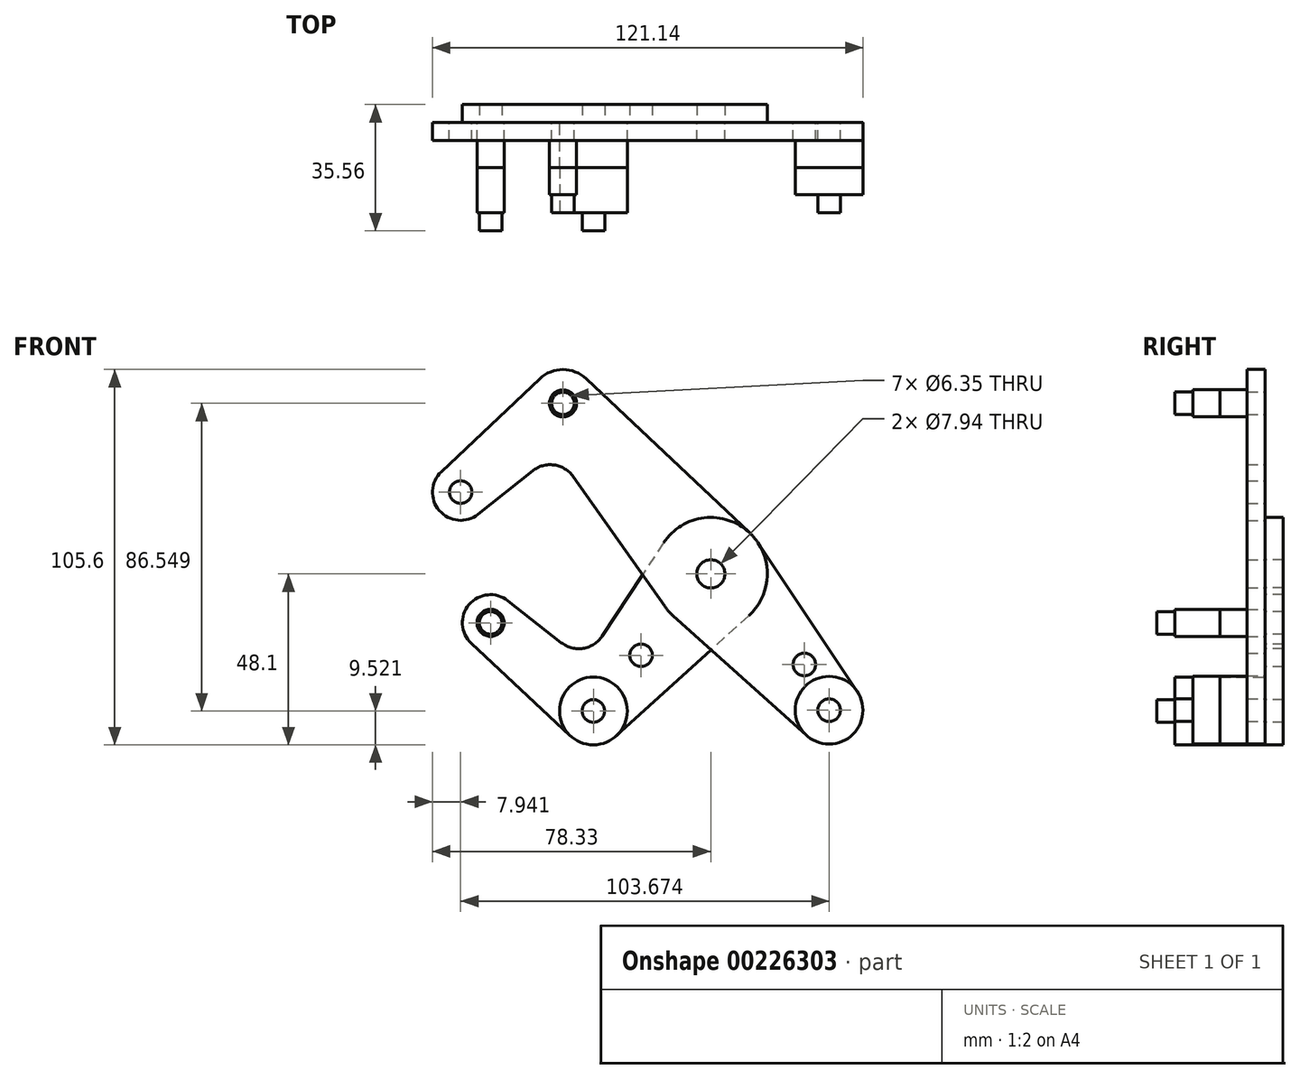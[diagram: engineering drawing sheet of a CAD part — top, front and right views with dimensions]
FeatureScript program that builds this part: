
annotation { "Feature Type Name" : "Feature", "Feature Type Description" : "" }
export const myFeature = defineFeature(function(context is Context, id is Id, definition is map)
    precondition{}
    {
        {
            var Q0;
            Q0=qCreatedBy(makeId("Front.planeOp"),FACE);
            var sketch = newSketch(context, id + "F0", { "sketchPlane" : qUnion([Q0])});
            skLineSegment(sketch, "E0", {"start": v(-41.6, 47.97) * mm, "end": v(41.6, -47.97) * mm, "construction": true});
            skCircle(sketch, "E1", {"center": v(0, 0) * mm, "radius": 3.18 * mm});
            skCircle(sketch, "E2", {"center": v(33.29, -38.38) * mm, "radius": 3.18 * mm});
            skCircle(sketch, "E3", {"center": v(-41.6, 47.97) * mm, "radius": 3.18 * mm});
            skCircle(sketch, "E4", {"center": v(-70.39, 23) * mm, "radius": 3.18 * mm});
            skLineSegment(sketch, "E5", {"start": v(-41.6, 47.97) * mm, "end": v(-70.39, 23) * mm, "construction": true});
            skCircle(sketch, "E6", {"center": v(33.29, -38.38) * mm, "radius": 9.53 * mm});
            skCircle(sketch, "E7", {"center": v(-70.39, 23) * mm, "radius": 7.94 * mm});
            skCircle(sketch, "E8", {"center": v(-41.6, 47.97) * mm, "radius": 9.53 * mm});
            skLineSegment(sketch, "E9", {"start": v(-75.83, 28.78) * mm, "end": v(-48.14, 54.9) * mm});
            skLineSegment(sketch, "E10", {"start": v(-65.44, 16.8) * mm, "end": v(-50.15, 28.98) * mm});
            skCircle(sketch, "E11", {"center": v(0, 0) * mm, "radius": 15.88 * mm});
            skLineSegment(sketch, "E12", {"start": v(-35.07, 54.9) * mm, "end": v(10.9, 11.55) * mm});
            skLineSegment(sketch, "E13", {"start": v(-38.72, 27.35) * mm, "end": v(-12.97, -9.15) * mm});
            skLineSegment(sketch, "E14", {"start": v(-10.6, -11.82) * mm, "end": v(26.93, -45.47) * mm});
            skLineSegment(sketch, "E15", {"start": v(13.2, 8.82) * mm, "end": v(41.2, -33.08) * mm});
            skArc(sketch, "E16.filletArc", {"start": v(-38.72, 27.35) * mm, "mid": v(-44.08, 30.63) * mm, "end": v(-50.15, 28.98) * mm});
            skLineSegment(sketch, "E17", {"start": v(0, 0) * mm, "end": v(-33.05, -38.58) * mm, "construction": true});
            skLineSegment(sketch, "E18", {"start": v(-33.05, -38.58) * mm, "end": v(-61.98, -13.8) * mm, "construction": true});
            skCircle(sketch, "E19", {"center": v(-61.98, -13.8) * mm, "radius": 3.18 * mm});
            skCircle(sketch, "E20", {"center": v(-33.05, -38.58) * mm, "radius": 3.18 * mm});
            skCircle(sketch, "E21", {"center": v(-61.98, -13.8) * mm, "radius": 7.94 * mm});
            skCircle(sketch, "E22", {"center": v(-33.05, -38.58) * mm, "radius": 9.53 * mm});
            skLineSegment(sketch, "E23", {"start": v(-57.08, -7.55) * mm, "end": v(-42.08, -19.35) * mm});
            skLineSegment(sketch, "E24", {"start": v(-67.4, -19.6) * mm, "end": v(-39.54, -45.55) * mm});
            skLineSegment(sketch, "E25", {"start": v(-13.25, 8.74) * mm, "end": v(-30.55, -17.48) * mm});
            skLineSegment(sketch, "E26", {"start": v(10.67, -11.75) * mm, "end": v(-26.65, -45.63) * mm});
            skArc(sketch, "E27.filletArc", {"start": v(-42.08, -19.35) * mm, "mid": v(-35.9, -20.95) * mm, "end": v(-30.55, -17.48) * mm});
            skCircle(sketch, "E28", {"center": v(-19.62, -22.9) * mm, "radius": 3.18 * mm});
            skCircle(sketch, "E29", {"center": v(26.32, -25.5) * mm, "radius": 3.18 * mm});
            skLineSegment(sketch, "E30", {"start": v(26.32, -25.5) * mm, "end": v(23.92, -27.58) * mm, "construction": true});
            skCircle(sketch, "E31", {"center": v(0, 0) * mm, "radius": 3.97 * mm});
            skSolve(sketch);
        }
        {
            var Q0;
            Q0=qCreatedBy(makeId("Front.planeOp"),FACE);
            cPlane(context, id + "F1", {"entities" : qUnion([Q0]), "cplaneType" : CPlaneType.OFFSET, "offset" : 12.7 * mm, "width" : 254 * mm, "height" : 254 * mm});
        }
        {
            var Q0;
            {var subQ0=sQuery(id+"F0.wireOp",EDGE,"E15");Q0=makeQuery(id+"F0.imprint","IMPRINT",FACE,{"disambiguationData":[TD([[makeQuery(id+"F0.imprint","IMPRINT",EDGE,{"derivedFrom":subQ0}),-1.0]])]});}
            var Q1;
            Q1=makeQuery(id+"F0.imprint","IMPRINT",FACE,{"disambiguationData":[TD([[makeQuery(id+"F0.imprint","IMPRINT",EDGE,{"derivedFrom":sQuery(id+"F0.wireOp",EDGE,"E31")}),-1.0]])]});
            var Q2;
            {var subQ1=sQuery(id+"F0.wireOp",EDGE,"E9");Q2=makeQuery(id+"F0.imprint","IMPRINT",FACE,{"disambiguationData":[TD([[makeQuery(id+"F0.imprint","IMPRINT",EDGE,{"derivedFrom":subQ1}),-1.0]])]});}
            var Q3;
            Q3=makeQuery(id+"F0.imprint","IMPRINT",FACE,{"disambiguationData":[TD([[makeQuery(id+"F0.imprint","IMPRINT",EDGE,{"derivedFrom":sQuery(id+"F0.wireOp",EDGE,"E2")}),-1.0]])]});
            var Q4;
            Q4=makeQuery(id+"F0.imprint","IMPRINT",FACE,{"disambiguationData":[TD([[makeQuery(id+"F0.imprint","IMPRINT",EDGE,{"derivedFrom":sQuery(id+"F0.wireOp",EDGE,"E3")}),-1.0]])]});
            var Q5;
            Q5=makeQuery(id+"F0.imprint","IMPRINT",FACE,{"disambiguationData":[TD([[makeQuery(id+"F0.imprint","IMPRINT",EDGE,{"derivedFrom":sQuery(id+"F0.wireOp",EDGE,"E4")}),-1.0]])]});
            var Q6;
            {var subQ0=sQuery(id+"F0.wireOp",EDGE,"E14");var subQ1=sQuery(id+"F0.wireOp",EDGE,"E11");var subQ2=makeQuery(id+"F0.imprint","INTERSECT",VERTEX,{"derivedFrom":[subQ1,subQ0]});Q6=makeQuery(id+"F0.imprint","IMPRINT",FACE,{"disambiguationData":[TD([[makeQuery(id+"F0.imprint","IMPRINT",EDGE,{"disambiguationData":[TD([[subQ2,-1.0]])],"derivedFrom":subQ1}),-1.0]])]});}
            var Q7;
            {var subQ0=sQuery(id+"F0.wireOp",EDGE,"E13");var subQ1=sQuery(id+"F0.wireOp",EDGE,"E11");var subQ2=makeQuery(id+"F0.imprint","INTERSECT",VERTEX,{"derivedFrom":[subQ1,subQ0]});Q7=makeQuery(id+"F0.imprint","IMPRINT",FACE,{"disambiguationData":[TD([[makeQuery(id+"F0.imprint","IMPRINT",EDGE,{"disambiguationData":[TD([[subQ2,1.0]])],"derivedFrom":subQ1}),-1.0]])]});}
            extrude(context, id + "F2", {"entities" : qUnion([Q0, Q1, Q2, Q3, Q4, Q5, Q6, Q7]), "depth" : 5.08 * mm});
        }
        {
            var Q0;
            {var subQ0=sQuery(id+"F0.wireOp",EDGE,"E14");var subQ1=sQuery(id+"F0.wireOp",EDGE,"E11");var subQ2=makeQuery(id+"F0.imprint","INTERSECT",VERTEX,{"derivedFrom":[subQ1,subQ0]});Q0=makeQuery(id+"F0.imprint","IMPRINT",FACE,{"disambiguationData":[TD([[makeQuery(id+"F0.imprint","IMPRINT",EDGE,{"disambiguationData":[TD([[subQ2,-1.0]])],"derivedFrom":subQ1}),-1.0]])]});}
            var Q1;
            {var subQ10=sQuery(id+"F0.wireOp",EDGE,"E23");Q1=makeQuery(id+"F0.imprint","IMPRINT",FACE,{"disambiguationData":[TD([[makeQuery(id+"F0.imprint","IMPRINT",EDGE,{"derivedFrom":subQ10}),-1.0]])]});}
            var Q2;
            Q2=makeQuery(id+"F0.imprint","IMPRINT",FACE,{"disambiguationData":[TD([[makeQuery(id+"F0.imprint","IMPRINT",EDGE,{"derivedFrom":sQuery(id+"F0.wireOp",EDGE,"E20")}),-1.0]])]});
            var Q3;
            Q3=makeQuery(id+"F0.imprint","IMPRINT",FACE,{"disambiguationData":[TD([[makeQuery(id+"F0.imprint","IMPRINT",EDGE,{"derivedFrom":sQuery(id+"F0.wireOp",EDGE,"E19")}),-1.0]])]});
            var Q4;
            Q4=makeQuery(id+"F0.imprint","IMPRINT",FACE,{"disambiguationData":[TD([[makeQuery(id+"F0.imprint","IMPRINT",EDGE,{"derivedFrom":sQuery(id+"F0.wireOp",EDGE,"E31")}),-1.0]])]});
            var Q5;
            {var subQ0=sQuery(id+"F0.wireOp",EDGE,"E13");var subQ1=sQuery(id+"F0.wireOp",EDGE,"E11");var subQ2=makeQuery(id+"F0.imprint","INTERSECT",VERTEX,{"derivedFrom":[subQ1,subQ0]});Q5=makeQuery(id+"F0.imprint","IMPRINT",FACE,{"disambiguationData":[TD([[makeQuery(id+"F0.imprint","IMPRINT",EDGE,{"disambiguationData":[TD([[subQ2,1.0]])],"derivedFrom":subQ1}),-1.0]])]});}
            extrude(context, id + "F3", {"entities" : qUnion([Q0, Q1, Q2, Q3, Q4, Q5]), "oppositeDirection" : true, "depth" : 5.08 * mm});
        }
        {
            var Q0;
            {var subQ1=sQuery(id+"F0.wireOp",EDGE,"E9");Q0=makeQuery(id+"F0.imprint","IMPRINT",FACE,{"disambiguationData":[TD([[makeQuery(id+"F0.imprint","IMPRINT",EDGE,{"derivedFrom":subQ1}),-1.0]])]});}
            var sketch = newSketch(context, id + "F4", { "sketchPlane" : qUnion([Q0])});
            skCircle(sketch, "E32.0", {"center": v(33.29, -38.38) * mm, "radius": 9.53 * mm});
            skCircle(sketch, "E33", {"center": v(-41.6, 47.97) * mm, "radius": 3.81 * mm});
            skSolve(sketch);
        }
        {
            var Q0;
            Q0=makeQuery(id+"F3.opExtrude","CAP_FACE",FACE,{"disambiguationData":[OSD([sQuery(id+"F0.wireOp",EDGE,"E11"),sQuery(id+"F0.wireOp",EDGE,"E19"),sQuery(id+"F0.wireOp",EDGE,"E20"),sQuery(id+"F0.wireOp",EDGE,"E21"),sQuery(id+"F0.wireOp",EDGE,"E22"),sQuery(id+"F0.wireOp",EDGE,"E23"),sQuery(id+"F0.wireOp",EDGE,"E24"),sQuery(id+"F0.wireOp",EDGE,"E25"),sQuery(id+"F0.wireOp",EDGE,"E26"),sQuery(id+"F0.wireOp",EDGE,"E27.filletArc"),sQuery(id+"F0.wireOp",EDGE,"E28"),sQuery(id+"F0.wireOp",EDGE,"E31")])],"isStart":false});
            var sketch = newSketch(context, id + "F5", { "sketchPlane" : qUnion([Q0])});
            skCircle(sketch, "E34.0", {"center": v(33.05, -38.58) * mm, "radius": 9.53 * mm});
            skCircle(sketch, "E35", {"center": v(61.98, -13.8) * mm, "radius": 3.81 * mm});
            skSolve(sketch);
        }
        {
            var Q0;
            Q0 = qSketchRegion(id + "F4", true);
            var Q1;
            Q1 = qSketchRegion(id + "F5", true);
            var Q2;
            Q2=qCreatedBy(id+"F1.planeOp",FACE);
            extrude(context, id + "F6", {"entities" : qUnion([Q0, Q1]), "endBound" : BoundingType.UP_TO_SURFACE, "endBoundEntityFace" : qUnion([Q2]), "depth" : 25.4 * mm});
        }
        {
            var Q0;
            Q0=makeQuery(id+"F2.opExtrude","SWEPT_BODY",BODY,{"disambiguationData":[OSD([sQuery(id+"F0.wireOp",EDGE,"E2"),sQuery(id+"F0.wireOp",EDGE,"E3"),sQuery(id+"F0.wireOp",EDGE,"E4"),sQuery(id+"F0.wireOp",EDGE,"E6"),sQuery(id+"F0.wireOp",EDGE,"E7"),sQuery(id+"F0.wireOp",EDGE,"E8"),sQuery(id+"F0.wireOp",EDGE,"E9"),sQuery(id+"F0.wireOp",EDGE,"E10"),sQuery(id+"F0.wireOp",EDGE,"E11"),sQuery(id+"F0.wireOp",EDGE,"E12"),sQuery(id+"F0.wireOp",EDGE,"E13"),sQuery(id+"F0.wireOp",EDGE,"E14"),sQuery(id+"F0.wireOp",EDGE,"E15"),sQuery(id+"F0.wireOp",EDGE,"E16.filletArc"),sQuery(id+"F0.wireOp",EDGE,"E29"),sQuery(id+"F0.wireOp",EDGE,"E31")])]});
            var Q1;
            Q1=makeQuery(id+"F3.opExtrude","SWEPT_BODY",BODY,{"disambiguationData":[OSD([sQuery(id+"F0.wireOp",EDGE,"E11"),sQuery(id+"F0.wireOp",EDGE,"E19"),sQuery(id+"F0.wireOp",EDGE,"E20"),sQuery(id+"F0.wireOp",EDGE,"E21"),sQuery(id+"F0.wireOp",EDGE,"E22"),sQuery(id+"F0.wireOp",EDGE,"E23"),sQuery(id+"F0.wireOp",EDGE,"E24"),sQuery(id+"F0.wireOp",EDGE,"E25"),sQuery(id+"F0.wireOp",EDGE,"E26"),sQuery(id+"F0.wireOp",EDGE,"E27.filletArc"),sQuery(id+"F0.wireOp",EDGE,"E28"),sQuery(id+"F0.wireOp",EDGE,"E31")])]});
            var Q2;
            Q2=makeQuery(id+"F6.opExtrude","SWEPT_BODY",BODY,{"disambiguationData":[OSD([sQuery(id+"F4.wireOp",EDGE,"E33")])]});
            var Q3;
            Q3=makeQuery(id+"F6.opExtrude","SWEPT_BODY",BODY,{"disambiguationData":[OSD([sQuery(id+"F5.wireOp",EDGE,"E35")])]});
            var Q4;
            Q4=makeQuery(id+"F6.opExtrude","SWEPT_BODY",BODY,{"disambiguationData":[OSD([sQuery(id+"F5.wireOp",EDGE,"E34.0")])]});
            var Q5;
            Q5=makeQuery(id+"F6.opExtrude","SWEPT_BODY",BODY,{"disambiguationData":[OSD([sQuery(id+"F4.wireOp",EDGE,"E32.0")])]});
            booleanBodies(context, id + "F7", {"operationType" : BooleanOperationType.SUBTRACTION, "tools" : qUnion([Q0, Q1]), "targets" : qUnion([Q2, Q3, Q4, Q5]), "keepTools" : true});
        }
        {
            var Q0;
            Q0=makeQuery(id+"F6.opExtrude","SWEPT_BODY",BODY,{"disambiguationData":[OSD([sQuery(id+"F4.wireOp",EDGE,"E32.0")])]});
            var Q1;
            Q1=makeQuery(id+"F6.opExtrude","SWEPT_BODY",BODY,{"disambiguationData":[OSD([sQuery(id+"F5.wireOp",EDGE,"E34.0")])]});
            var Q2;
            Q2=makeQuery(id+"F6.opExtrude","SWEPT_BODY",BODY,{"disambiguationData":[OSD([sQuery(id+"F4.wireOp",EDGE,"E33")])]});
            var Q3;
            Q3=makeQuery(id+"F6.opExtrude","SWEPT_BODY",BODY,{"disambiguationData":[OSD([sQuery(id+"F5.wireOp",EDGE,"E35")])]});
            var Q4;
            Q4=qCreatedBy(id+"F1.planeOp",FACE);
            mirror(context, id + "F8", {"entities" : qUnion([Q0, Q1, Q2, Q3]), "mirrorPlane" : qUnion([Q4])});
        }
    });
